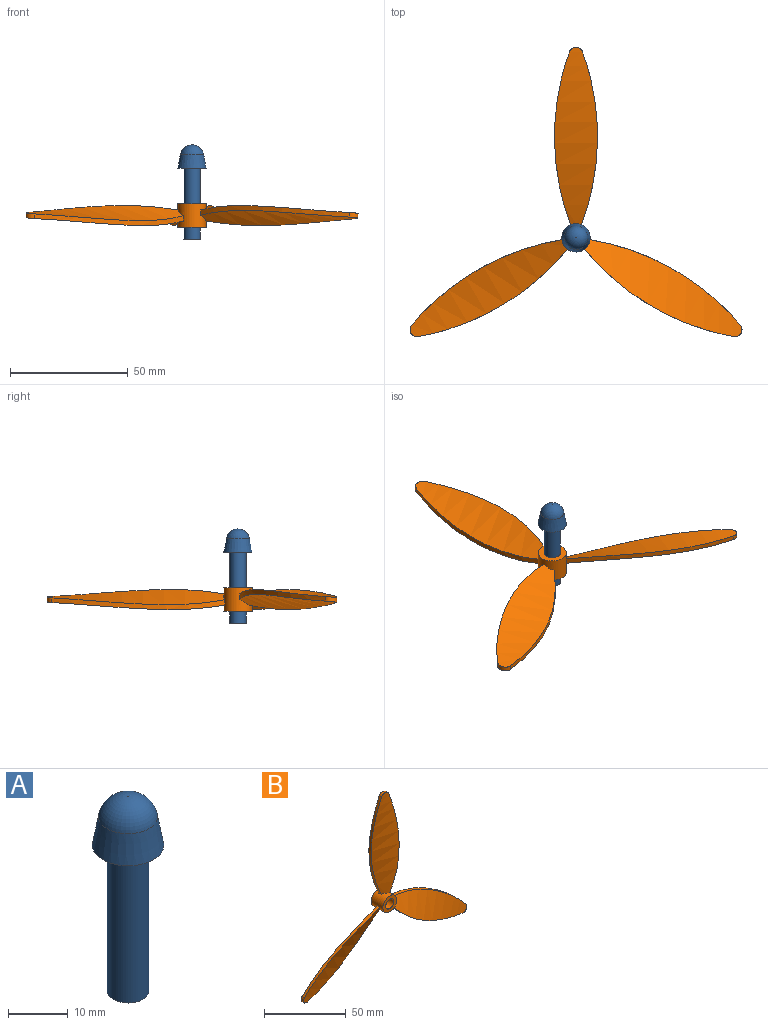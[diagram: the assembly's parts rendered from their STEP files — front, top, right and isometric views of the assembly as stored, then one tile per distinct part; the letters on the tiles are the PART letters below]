
ASSEMBLY  parts=2 mates=1
PART A: 6 faces, bbox 12x12x40 mm
  f0: cylinder r=3.5mm len=30mm, axis (0,0,-1), area 659.7mm2, adj f1,f4
  f1: plane 7x7mm, normal (0,0,-1), area 38.5mm2, adj f0
  f2: cone r=6mm half-angle=10deg, axis (0,0,-1), area 205.3mm2, adj f4,f5
  f3: plane 0.08x0.08mm, normal (0,0,1), area 0mm2, adj f5
  f4: plane 12x12mm, normal (0,0,-1), area 74.6mm2, adj f0,f2
  f5: torus R=0.04mm, axis (0,0,1), area 131.6mm2, adj f2,f3
PART B: 19 faces, bbox 188.2x16.7x163 mm
  f0: bspline ~100x30mm, area 1083.3mm2, adj f1,f2,f4,f15
  f1: cylinder r=106mm len=73.47mm, axis (0,1,0), area 154.2mm2, adj f0,f3,f4,f15
  f2: cylinder r=106mm len=73.47mm, axis (0,1,0), area 154.2mm2, adj f0,f3,f4,f15
  f3: bspline ~100x30mm, area 1083.3mm2, adj f1,f2,f4,f15
  f4: cylinder r=3mm len=5.64mm, axis (0,1,0), area 14.4mm2, adj f0,f1,f2,f3
  f5: bspline ~100.35x74.67mm, area 1083.3mm2, adj f6,f7,f9,f15
  f6: cylinder r=106mm len=63.35mm, axis (0,1,0), area 154.2mm2, adj f5,f8,f9,f15
  f7: cylinder r=106mm len=63.9mm, axis (0,1,0), area 154.2mm2, adj f5,f8,f9,f15
  f8: bspline ~100.85x73.81mm, area 1083.3mm2, adj f6,f7,f9,f15
  f9: cylinder r=3mm len=4.93mm, axis (0,1,0), area 14.4mm2, adj f5,f6,f7,f8
  f10: bspline ~100.85x73.81mm, area 1083.3mm2, adj f11,f12,f14,f15
  f11: cylinder r=106mm len=63.9mm, axis (0,1,0), area 154.2mm2, adj f10,f13,f14,f15
  f12: cylinder r=106mm len=63.35mm, axis (0,1,0), area 154.2mm2, adj f10,f13,f14,f15
  f13: bspline ~100.35x74.67mm, area 1083.3mm2, adj f11,f12,f14,f15
  f14: cylinder r=3mm len=4.93mm, axis (0,1,0), area 14.4mm2, adj f10,f11,f12,f13
  f15: cylinder r=6mm len=12mm, axis (0,1,0), area 345.3mm2, adj f0,f1,f2,f3,f5,f6,f7,f8
  f16: plane 12x12mm, normal (0,-1,0), area 74.6mm2, adj f15,f18
  f17: plane 12x12mm, normal (0,1,0), area 74.6mm2, adj f15,f18
  f18: cylinder r=3.5mm len=10mm, axis (0,-1,0), area 219.9mm2, adj f16,f17
PLACE A t=(31.53,35.1,5.35)mm fixed
PLACE B rot(axis=(-1,0,0),90deg) t=(31.53,35.1,15.35)mm
MATE revolute A.f0 <-> B.f18  axis (0,0,-1) through (31.53,35.1,20.35)mm
